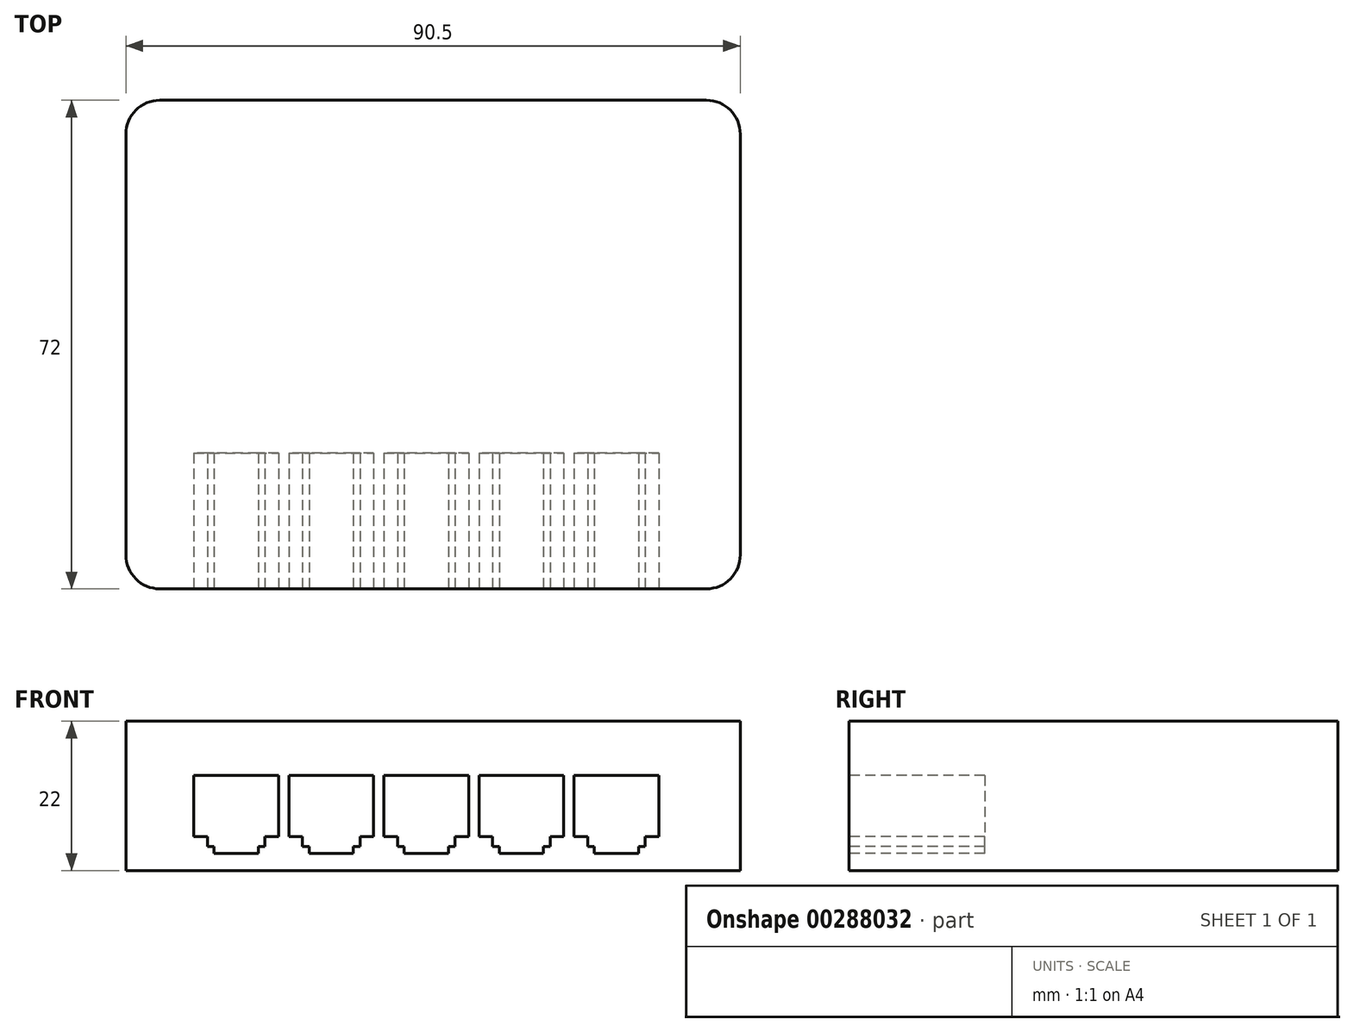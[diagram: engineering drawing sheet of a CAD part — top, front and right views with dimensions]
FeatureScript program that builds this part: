
annotation { "Feature Type Name" : "Feature", "Feature Type Description" : "" }
export const myFeature = defineFeature(function(context is Context, id is Id, definition is map)
    precondition{}
    {
        {
            var Q0;
            Q0=qCreatedBy(makeId("Top.planeOp"),FACE);
            var sketch = newSketch(context, id + "F0", { "sketchPlane" : qUnion([Q0])});
            skLineSegment(sketch, "E0.bottom", {"start": v(40.25, -36) * mm, "end": v(-40.25, -36) * mm});
            skLineSegment(sketch, "E0.top", {"start": v(40.25, 36) * mm, "end": v(-40.25, 36) * mm});
            skLineSegment(sketch, "E0.left", {"start": v(45.25, -31) * mm, "end": v(45.25, 31) * mm});
            skLineSegment(sketch, "E0.right", {"start": v(-45.25, -31) * mm, "end": v(-45.25, 31) * mm});
            skPoint(sketch, "E0.middle", {"position": v(0, 0) * mm});
            skPoint(sketch, "E1.visualSharp", {"position": v(-45.25, 36) * mm});
            skArc(sketch, "E1.filletArc", {"start": v(-40.25, 36) * mm, "mid": v(-43.79, 34.54) * mm, "end": v(-45.25, 31) * mm});
            skPoint(sketch, "E2.visualSharp", {"position": v(45.25, 36) * mm});
            skArc(sketch, "E2.filletArc", {"start": v(45.25, 31) * mm, "mid": v(43.79, 34.54) * mm, "end": v(40.25, 36) * mm});
            skPoint(sketch, "E3.visualSharp", {"position": v(45.25, -36) * mm});
            skArc(sketch, "E3.filletArc", {"start": v(40.25, -36) * mm, "mid": v(43.79, -34.54) * mm, "end": v(45.25, -31) * mm});
            skPoint(sketch, "E4.visualSharp", {"position": v(-45.25, -36) * mm});
            skArc(sketch, "E4.filletArc", {"start": v(-45.25, -31) * mm, "mid": v(-43.79, -34.54) * mm, "end": v(-40.25, -36) * mm});
            skSolve(sketch);
        }
        {
            var Q0;
            Q0 = qSketchRegion(id + "F0", true);
            extrude(context, id + "F1", {"entities" : qUnion([Q0]), "depth" : 22 * mm});
        }
        {
            var Q0;
            Q0=makeQuery(id+"F1.opExtrude","SWEPT_FACE",FACE,{"disambiguationData":[OSD([sQuery(id+"F0.wireOp",EDGE,"E0.bottom")])]});
            var sketch = newSketch(context, id + "F2", { "sketchPlane" : qUnion([Q0])});
            skLineSegment(sketch, "E5", {"start": v(-35.25, 14) * mm, "end": v(-22.75, 14) * mm});
            skLineSegment(sketch, "E6", {"start": v(-22.75, 14) * mm, "end": v(-22.75, 5) * mm});
            skLineSegment(sketch, "E7", {"start": v(-22.75, 5) * mm, "end": v(-24.75, 5) * mm});
            skLineSegment(sketch, "E8", {"start": v(-24.75, 5) * mm, "end": v(-24.75, 3.5) * mm});
            skLineSegment(sketch, "E9", {"start": v(-24.75, 3.5) * mm, "end": v(-25.75, 3.5) * mm});
            skLineSegment(sketch, "E10", {"start": v(-25.75, 3.5) * mm, "end": v(-25.75, 2.5) * mm});
            skLineSegment(sketch, "E11", {"start": v(-25.75, 2.5) * mm, "end": v(-32.25, 2.5) * mm});
            skLineSegment(sketch, "E12", {"start": v(-32.25, 2.5) * mm, "end": v(-32.25, 3.5) * mm});
            skLineSegment(sketch, "E13", {"start": v(-32.25, 3.5) * mm, "end": v(-33.25, 3.5) * mm});
            skLineSegment(sketch, "E14", {"start": v(-33.25, 3.5) * mm, "end": v(-33.25, 5) * mm});
            skLineSegment(sketch, "E15", {"start": v(-33.25, 5) * mm, "end": v(-35.25, 5) * mm});
            skLineSegment(sketch, "E16", {"start": v(-35.25, 5) * mm, "end": v(-35.25, 14) * mm});
            skLineSegment(sketch, "E17.1.0.0", {"start": v(-21.25, 14) * mm, "end": v(-8.75, 14) * mm});
            skLineSegment(sketch, "E17.1.0.1", {"start": v(-8.75, 14) * mm, "end": v(-8.75, 5) * mm});
            skLineSegment(sketch, "E17.1.0.2", {"start": v(-21.25, 5) * mm, "end": v(-21.25, 14) * mm});
            skLineSegment(sketch, "E17.1.0.3", {"start": v(-19.25, 5) * mm, "end": v(-21.25, 5) * mm});
            skLineSegment(sketch, "E17.1.0.4", {"start": v(-8.75, 5) * mm, "end": v(-10.75, 5) * mm});
            skLineSegment(sketch, "E17.1.0.5", {"start": v(-19.25, 3.5) * mm, "end": v(-19.25, 5) * mm});
            skLineSegment(sketch, "E17.1.0.6", {"start": v(-10.75, 5) * mm, "end": v(-10.75, 3.5) * mm});
            skLineSegment(sketch, "E17.1.0.7", {"start": v(-11.75, 2.5) * mm, "end": v(-18.25, 2.5) * mm});
            skLineSegment(sketch, "E17.1.0.8", {"start": v(-10.75, 3.5) * mm, "end": v(-11.75, 3.5) * mm});
            skLineSegment(sketch, "E17.1.0.9", {"start": v(-18.25, 3.5) * mm, "end": v(-19.25, 3.5) * mm});
            skLineSegment(sketch, "E17.1.0.10", {"start": v(-11.75, 3.5) * mm, "end": v(-11.75, 2.5) * mm});
            skLineSegment(sketch, "E17.1.0.11", {"start": v(-18.25, 2.5) * mm, "end": v(-18.25, 3.5) * mm});
            skLineSegment(sketch, "E17.2.0.0", {"start": v(-7.25, 14) * mm, "end": v(5.25, 14) * mm});
            skLineSegment(sketch, "E17.2.0.1", {"start": v(5.25, 14) * mm, "end": v(5.25, 5) * mm});
            skLineSegment(sketch, "E17.2.0.2", {"start": v(-7.25, 5) * mm, "end": v(-7.25, 14) * mm});
            skLineSegment(sketch, "E17.2.0.3", {"start": v(-5.25, 5) * mm, "end": v(-7.25, 5) * mm});
            skLineSegment(sketch, "E17.2.0.4", {"start": v(5.25, 5) * mm, "end": v(3.25, 5) * mm});
            skLineSegment(sketch, "E17.2.0.5", {"start": v(-5.25, 3.5) * mm, "end": v(-5.25, 5) * mm});
            skLineSegment(sketch, "E17.2.0.6", {"start": v(3.25, 5) * mm, "end": v(3.25, 3.5) * mm});
            skLineSegment(sketch, "E17.2.0.7", {"start": v(2.25, 2.5) * mm, "end": v(-4.25, 2.5) * mm});
            skLineSegment(sketch, "E17.2.0.8", {"start": v(3.25, 3.5) * mm, "end": v(2.25, 3.5) * mm});
            skLineSegment(sketch, "E17.2.0.9", {"start": v(-4.25, 3.5) * mm, "end": v(-5.25, 3.5) * mm});
            skLineSegment(sketch, "E17.2.0.10", {"start": v(2.25, 3.5) * mm, "end": v(2.25, 2.5) * mm});
            skLineSegment(sketch, "E17.2.0.11", {"start": v(-4.25, 2.5) * mm, "end": v(-4.25, 3.5) * mm});
            skLineSegment(sketch, "E17.3.0.0", {"start": v(6.75, 14) * mm, "end": v(19.25, 14) * mm});
            skLineSegment(sketch, "E17.3.0.1", {"start": v(19.25, 14) * mm, "end": v(19.25, 5) * mm});
            skLineSegment(sketch, "E17.3.0.2", {"start": v(6.75, 5) * mm, "end": v(6.75, 14) * mm});
            skLineSegment(sketch, "E17.3.0.3", {"start": v(8.75, 5) * mm, "end": v(6.75, 5) * mm});
            skLineSegment(sketch, "E17.3.0.4", {"start": v(19.25, 5) * mm, "end": v(17.25, 5) * mm});
            skLineSegment(sketch, "E17.3.0.5", {"start": v(8.75, 3.5) * mm, "end": v(8.75, 5) * mm});
            skLineSegment(sketch, "E17.3.0.6", {"start": v(17.25, 5) * mm, "end": v(17.25, 3.5) * mm});
            skLineSegment(sketch, "E17.3.0.7", {"start": v(16.25, 2.5) * mm, "end": v(9.75, 2.5) * mm});
            skLineSegment(sketch, "E17.3.0.8", {"start": v(17.25, 3.5) * mm, "end": v(16.25, 3.5) * mm});
            skLineSegment(sketch, "E17.3.0.9", {"start": v(9.75, 3.5) * mm, "end": v(8.75, 3.5) * mm});
            skLineSegment(sketch, "E17.3.0.10", {"start": v(16.25, 3.5) * mm, "end": v(16.25, 2.5) * mm});
            skLineSegment(sketch, "E17.3.0.11", {"start": v(9.75, 2.5) * mm, "end": v(9.75, 3.5) * mm});
            skLineSegment(sketch, "E17.4.0.0", {"start": v(20.75, 14) * mm, "end": v(33.25, 14) * mm});
            skLineSegment(sketch, "E17.4.0.1", {"start": v(33.25, 14) * mm, "end": v(33.25, 5) * mm});
            skLineSegment(sketch, "E17.4.0.2", {"start": v(20.75, 5) * mm, "end": v(20.75, 14) * mm});
            skLineSegment(sketch, "E17.4.0.3", {"start": v(22.75, 5) * mm, "end": v(20.75, 5) * mm});
            skLineSegment(sketch, "E17.4.0.4", {"start": v(33.25, 5) * mm, "end": v(31.25, 5) * mm});
            skLineSegment(sketch, "E17.4.0.5", {"start": v(22.75, 3.5) * mm, "end": v(22.75, 5) * mm});
            skLineSegment(sketch, "E17.4.0.6", {"start": v(31.25, 5) * mm, "end": v(31.25, 3.5) * mm});
            skLineSegment(sketch, "E17.4.0.7", {"start": v(30.25, 2.5) * mm, "end": v(23.75, 2.5) * mm});
            skLineSegment(sketch, "E17.4.0.8", {"start": v(31.25, 3.5) * mm, "end": v(30.25, 3.5) * mm});
            skLineSegment(sketch, "E17.4.0.9", {"start": v(23.75, 3.5) * mm, "end": v(22.75, 3.5) * mm});
            skLineSegment(sketch, "E17.4.0.10", {"start": v(30.25, 3.5) * mm, "end": v(30.25, 2.5) * mm});
            skLineSegment(sketch, "E17.4.0.11", {"start": v(23.75, 2.5) * mm, "end": v(23.75, 3.5) * mm});
            skLineSegment(sketch, "E17.direction1", {"start": v(-35.25, 5) * mm, "end": v(-21.25, 5) * mm, "construction": true});
            skSolve(sketch);
        }
        {
            var Q0;
            Q0 = qSketchRegion(id + "F2", true);
            extrude(context, id + "F3", {"entities" : qUnion([Q0]), "operationType" : NewBodyOperationType.REMOVE, "oppositeDirection" : true, "depth" : 20 * mm});
        }
    });
